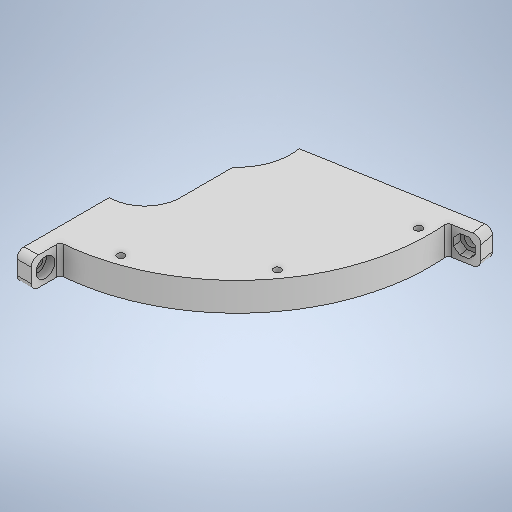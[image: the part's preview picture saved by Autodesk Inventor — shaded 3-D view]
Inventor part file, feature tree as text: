
AUTODESK INVENTOR PART (.ipt)
format: ipt  version: 2025 (Build 290162000, 162)  size: 405,504 bytes
history: native  units: in
note: dims shown in document units (in); Inventor stores cm internally (conversion verified against a paired STEP export)
features: sketch x15, extrude x11, hole x3, fillet x1
ambient origin geometry x8: Origin, YZ Plane, XZ Plane, XY Plane, X Axis, Y Axis, Z Axis, Center Point
bodies: Solid1 (feature_tree)
feature tree (30):
  extrude  "Extrusion1"  Depth=8.6614in
  extrude  "Extrusion2"  Depth=2.1654in
  extrude  "Extrusion3"  TaperAngle=0.0deg  [1 undecoded]
  extrude  "Extrusion4"  Depth=2.7559in
  hole  "Hole1"  [1 undecoded]
  extrude  "Extrusion5"  Depth=10.0394in
  extrude  "Extrusion6"  Depth=0.1575in TaperAngle=360.0deg
  extrude  "Extrusion7"  Depth=0.5906in TaperAngle=0.0deg
  extrude  "Extrusion8"  Depth=0.5512in TaperAngle=0.0deg
  extrude  "Extrusion9"  TaperAngle=0.0deg  [1 undecoded]
  extrude  "Extrusion10"  Depth=0.7874in
  fillet  "Fillet1"  Radius=0.7874in
  hole  "Hole2"  [1 undecoded]
  extrude  "Extrusion11"  Depth=0.7874in
  hole  "Hole3"  [1 undecoded]
  sketch  "Sketch1"  dims[d0=10.6299in d1=8.6614in]
  sketch  "Sketch2"  dims[d5=0.1969in d6=0.0in d7=0.0in]
  sketch  "Sketch3"  dims[d8=0.7874in d9=0.0in d10=2.7559in]
  sketch  "Sketch4"  dims[d11=0.7874in d12=7.874in]
  sketch  "Sketch5"  dims[d13=0.0in d14=0.0in d15=10.0394in]
  sketch  "Sketch Circular Pattern1"  dims[d2=2.1654in d3=0.0in d4=1.4173in]
  sketch  "Sketch6"  dims[d16=0.1575in d17=3.937in d19=360.0deg]
  sketch  "Sketch7"  dims[d21=0.1969in d22=0.3937in d23=0.4094in d24=0.0787in d25=90.0deg d26=0.315in d27=0.8108in d28=0.5906in d29=0.0in]
  sketch  "Sketch8"  dims[d30=2.9528in d33=0.0394in d34=0.0in d38=0.5512in d39=0.0in]
  sketch  "Sketch9"  dims[d40=0.5497in d41=0.0in d42=0.0in]
  sketch  "Sketch10"  dims[d43=0.8858in d44=0.7874in d45=0.7874in]
  sketch  "Sketch11"  dims[d46=0.1969in d47=0.3937in d48=0.0in]
  sketch  "Sketch12"  dims[d49=0.8858in d50=0.7874in]
  sketch  "Sketch13"  dims[d51=0.7874in d52=0.1969in]
  sketch  "Sketch14"  dims[d53=0.3937in d54=0.0in d55=0.0984in d56=0.3937in d57=0.3937in d58=0.3228in d59=0.2362in d60=0.5197in d61=0.2362in d62=90.0deg d63=0.315in d64=0.8108in d65=0.3937in d66=0.3937in d67=0.5197in d68=0.2362in d69=0.0in d70=0.3937in d71=0.3937in d72=0.3228in d73=0.2362in d74=0.5197in d75=0.2362in d76=90.0deg d77=0.315in d78=0.8108in]
note: 5 required parameter values undecoded (feature->parameter linkage not recoverable at this tier; creation-order binding heuristic only, values carry confidence <= 0.55)
